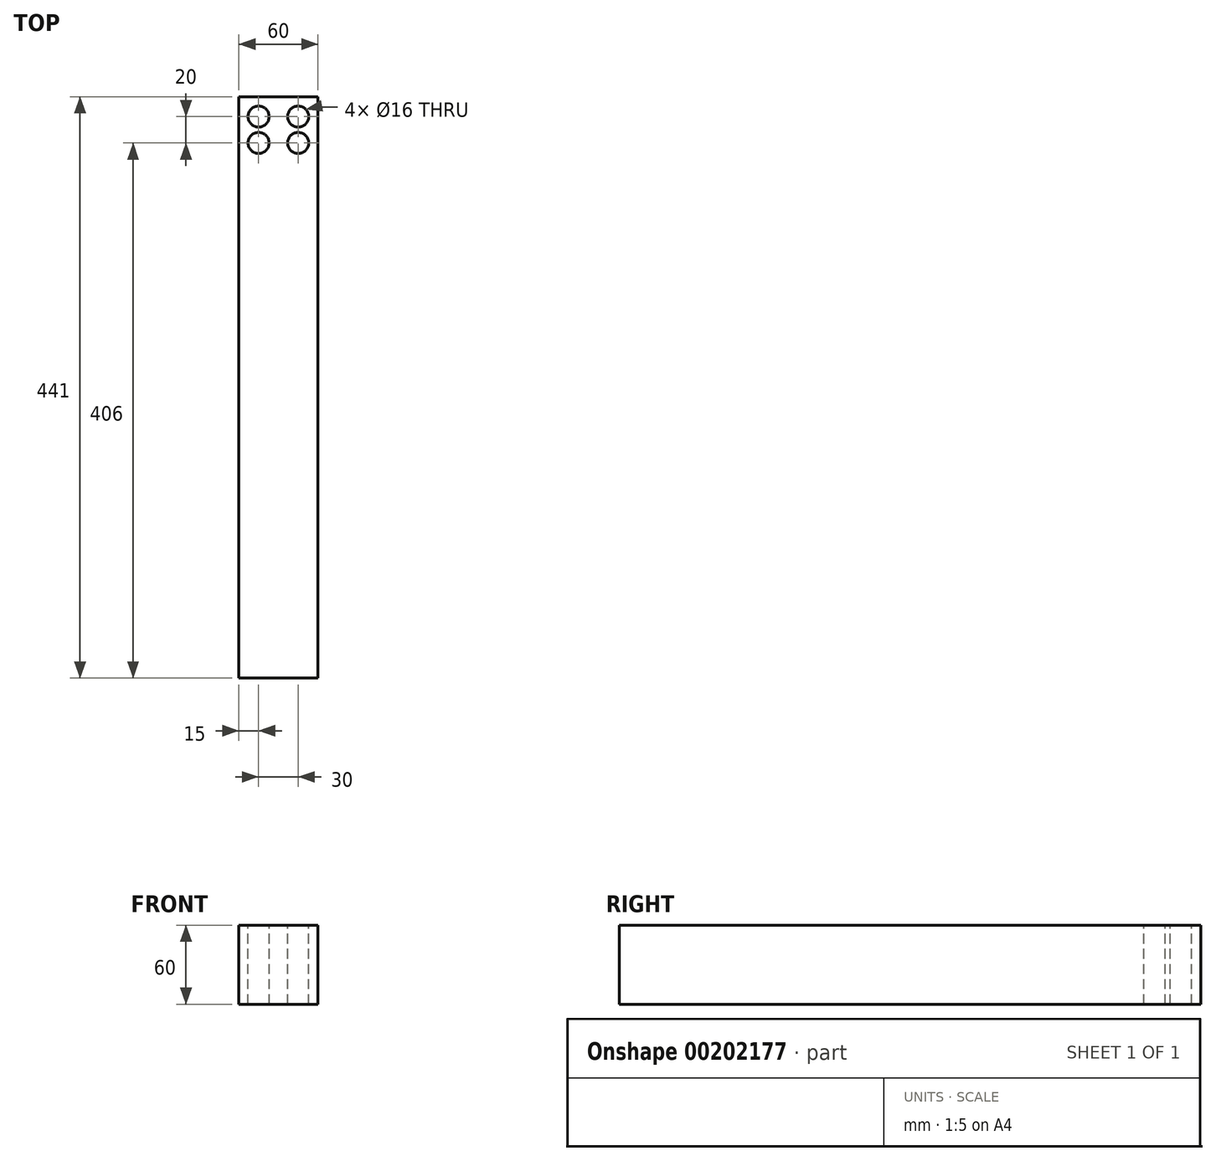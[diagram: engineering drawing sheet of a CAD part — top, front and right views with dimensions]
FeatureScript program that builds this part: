
annotation { "Feature Type Name" : "Feature", "Feature Type Description" : "" }
export const myFeature = defineFeature(function(context is Context, id is Id, definition is map)
    precondition{}
    {
        {
            var Q0;
            Q0=qCreatedBy(makeId("Front.planeOp"),FACE);
            var sketch = newSketch(context, id + "F0", { "sketchPlane" : qUnion([Q0])});
            skLineSegment(sketch, "E0.bottom", {"start": v(30, -30) * mm, "end": v(-30, -30) * mm});
            skLineSegment(sketch, "E0.top", {"start": v(30, 30) * mm, "end": v(-30, 30) * mm});
            skLineSegment(sketch, "E0.left", {"start": v(30, -30) * mm, "end": v(30, 30) * mm});
            skLineSegment(sketch, "E0.right", {"start": v(-30, -30) * mm, "end": v(-30, 30) * mm});
            skPoint(sketch, "E0.middle", {"position": v(0, 0) * mm});
            skSolve(sketch);
        }
        {
            var Q0;
            Q0=qSketchRegion(id+"F0",true);
            extrude(context, id + "F1", {"entities" : qUnion([Q0]), "depth" : 441 * mm});
        }
        {
            var Q0;
            Q0=makeQuery(id+"F1.opExtrude","SWEPT_FACE",FACE,{"disambiguationData":[OSD([sQuery(id+"F0.wireOp",EDGE,"E0.top")])]});
            var sketch = newSketch(context, id + "F2", { "sketchPlane" : qUnion([Q0])});
            skLineSegment(sketch, "E1", {"start": v(0, 0) * mm, "end": v(0, -15) * mm, "construction": true});
            skPoint(sketch, "E1.endSnap0", {"position": v(0, 0) * mm});
            skLineSegment(sketch, "E2", {"start": v(0, -15) * mm, "end": v(0, -35) * mm, "construction": true});
            skLineSegment(sketch, "E3", {"start": v(0, -15) * mm, "end": v(-15, -15) * mm, "construction": true});
            skLineSegment(sketch, "E4", {"start": v(-15, -15) * mm, "end": v(-15, -35) * mm, "construction": true});
            skLineSegment(sketch, "E5", {"start": v(-15, -35) * mm, "end": v(0, -35) * mm, "construction": true});
            skLineSegment(sketch, "E6", {"start": v(0, -35) * mm, "end": v(15, -35) * mm, "construction": true});
            skLineSegment(sketch, "E7", {"start": v(15, -35) * mm, "end": v(15, -15) * mm, "construction": true});
            skLineSegment(sketch, "E8", {"start": v(15, -15) * mm, "end": v(0, -15) * mm, "construction": true});
            skSolve(sketch);
        }
        {
            var Q0;
            Q0=sQuery(id+"F2.wireOp",VERTEX,"E4.start");
            var Q1;
            Q1=sQuery(id+"F2.wireOp",VERTEX,"E8.start");
            var Q2;
            Q2=sQuery(id+"F2.wireOp",VERTEX,"E5.start");
            var Q3;
            Q3=sQuery(id+"F2.wireOp",VERTEX,"E7.start");
            var Q4;
            Q4=makeQuery(id+"F1.opExtrude","SWEPT_BODY",BODY,{"disambiguationData":[OSD([sQuery(id+"F0.wireOp",EDGE,"E0.bottom"),sQuery(id+"F0.wireOp",EDGE,"E0.top"),sQuery(id+"F0.wireOp",EDGE,"E0.left"),sQuery(id+"F0.wireOp",EDGE,"E0.right")])]});
            hole(context, id + "F3", {"style" : HoleStyle.SIMPLE, "endStyle" : HoleEndStyle.THROUGH, "holeDiameter" : 16 * mm, "locations" : qUnion([Q0, Q1, Q2, Q3]), "scope" : qUnion([Q4]), "isTappedThrough" : true});
        }
    });
